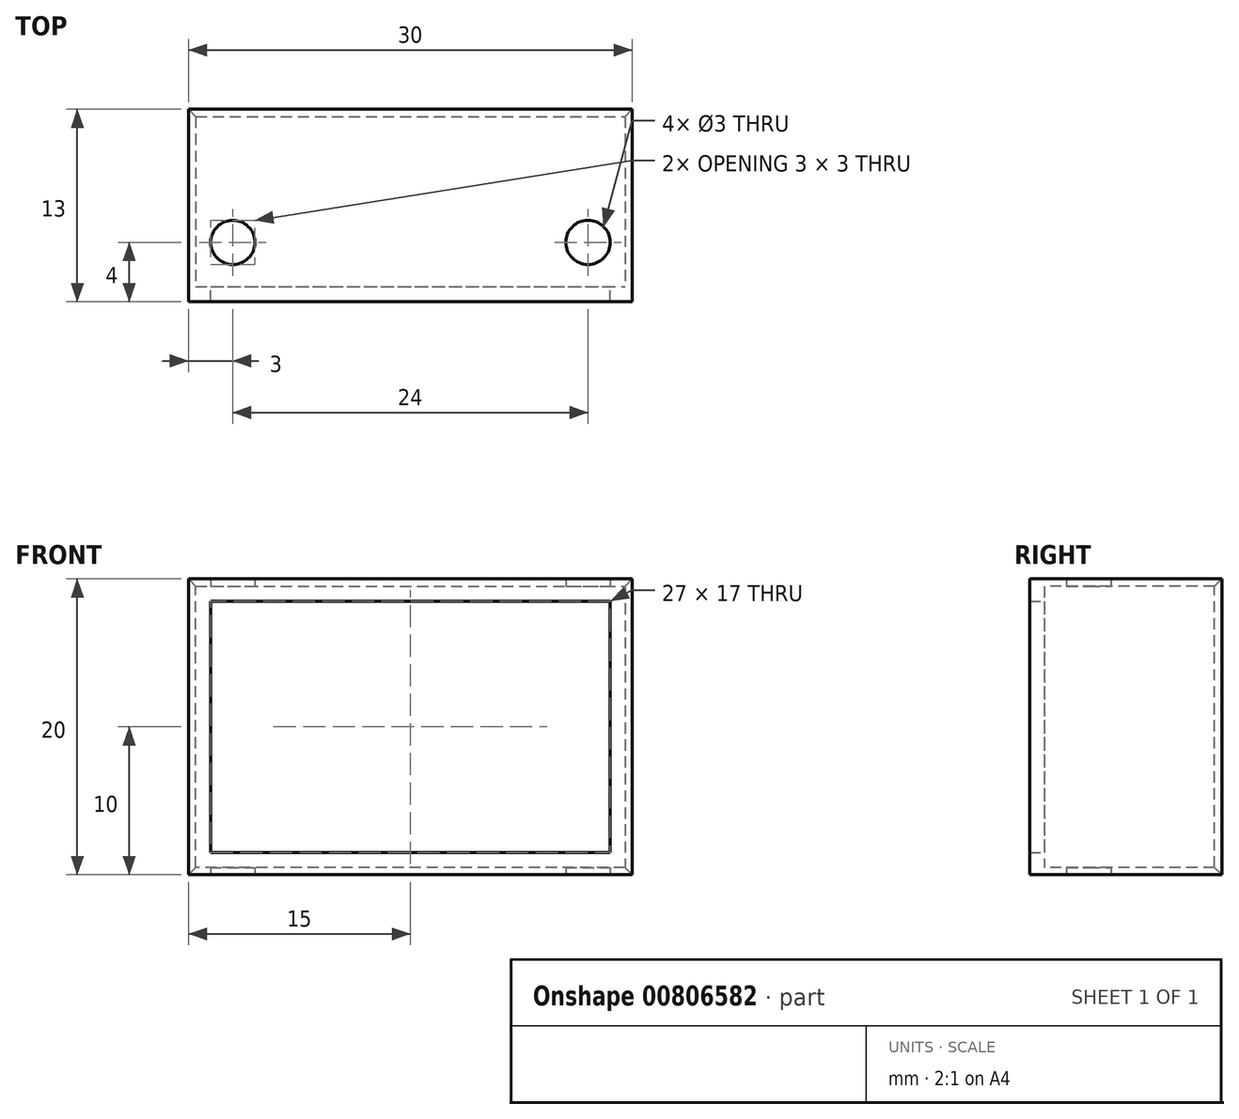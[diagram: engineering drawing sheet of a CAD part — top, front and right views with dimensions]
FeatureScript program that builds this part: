
annotation { "Feature Type Name" : "Feature", "Feature Type Description" : "" }
export const myFeature = defineFeature(function(context is Context, id is Id, definition is map)
    precondition{}
    {
        {
            var Q0;
            Q0=qCreatedBy(makeId("Top.planeOp"),FACE);
            var sketch = newSketch(context, id + "F0", { "sketchPlane" : qUnion([Q0])});
            skLineSegment(sketch, "E0.bottom", {"start": v(-15, 12) * mm, "end": v(15, 12) * mm});
            skLineSegment(sketch, "E0.top", {"start": v(-15, 0) * mm, "end": v(15, 0) * mm});
            skLineSegment(sketch, "E0.left", {"start": v(-15, 12) * mm, "end": v(-15, 0) * mm});
            skLineSegment(sketch, "E0.right", {"start": v(15, 12) * mm, "end": v(15, 0) * mm});
            skCircle(sketch, "E1", {"center": v(-12, 3) * mm, "radius": 1.5 * mm});
            skCircle(sketch, "E2", {"center": v(12, 3) * mm, "radius": 1.5 * mm});
            skSolve(sketch);
        }
        {
            var Q0;
            Q0=makeQuery(id+"F0.imprint","IMPRINT",FACE,{"disambiguationData":[TD([[makeQuery(id+"F0.imprint","IMPRINT",EDGE,{"derivedFrom":sQuery(id+"F0.wireOp",EDGE,"E0.bottom")}),-1.0]])]});
            extrude(context, id + "F1", {"entities" : qUnion([Q0]), "depth" : 20 * mm, "offsetDistance" : 25 * mm});
        }
        {
            var Q0;
            Q0=qCreatedBy(makeId("Front.planeOp"),FACE);
            var sketch = newSketch(context, id + "F2", { "sketchPlane" : qUnion([Q0])});
            skLineSegment(sketch, "E3.bottom", {"start": v(-14.5, 19.5) * mm, "end": v(14.5, 19.5) * mm});
            skLineSegment(sketch, "E3.top", {"start": v(-14.5, 0.5) * mm, "end": v(14.5, 0.5) * mm});
            skLineSegment(sketch, "E3.left", {"start": v(-14.5, 19.5) * mm, "end": v(-14.5, 0.5) * mm});
            skLineSegment(sketch, "E3.right", {"start": v(14.5, 19.5) * mm, "end": v(14.5, 0.5) * mm});
            skLineSegment(sketch, "E4.0", {"start": v(-13.5, 18.5) * mm, "end": v(13.5, 18.5) * mm});
            skLineSegment(sketch, "E4.1", {"start": v(-13.5, 18.5) * mm, "end": v(-13.5, 1.5) * mm});
            skLineSegment(sketch, "E4.2", {"start": v(-13.5, 1.5) * mm, "end": v(13.5, 1.5) * mm});
            skLineSegment(sketch, "E4.3", {"start": v(13.5, 18.5) * mm, "end": v(13.5, 1.5) * mm});
            skLineSegment(sketch, "E5.0", {"start": v(-15, 20) * mm, "end": v(15, 20) * mm});
            skLineSegment(sketch, "E5.1", {"start": v(-15, 20) * mm, "end": v(-15, 0) * mm});
            skLineSegment(sketch, "E5.2", {"start": v(-15, 0) * mm, "end": v(15, 0) * mm});
            skLineSegment(sketch, "E5.3", {"start": v(15, 20) * mm, "end": v(15, 0) * mm});
            skSolve(sketch);
        }
        {
            var Q0;
            Q0=makeQuery(id+"F2.imprint","IMPRINT",FACE,{"disambiguationData":[TD([[makeQuery(id+"F2.imprint","IMPRINT",EDGE,{"derivedFrom":sQuery(id+"F2.wireOp",EDGE,"E3.bottom")}),-1.0]])]});
            var Q1;
            Q1=makeQuery(id+"F2.imprint","IMPRINT",FACE,{"disambiguationData":[TD([[makeQuery(id+"F2.imprint","IMPRINT",EDGE,{"derivedFrom":sQuery(id+"F2.wireOp",EDGE,"E4.0")}),-1.0]])]});
            extrude(context, id + "F3", {"entities" : qUnion([Q0, Q1]), "operationType" : NewBodyOperationType.REMOVE, "oppositeDirection" : true, "depth" : 12 * mm, "offsetDistance" : 25 * mm});
        }
        {
            var Q0;
            Q0=makeQuery(id+"F2.imprint","IMPRINT",FACE,{"disambiguationData":[TD([[makeQuery(id+"F2.imprint","IMPRINT",EDGE,{"derivedFrom":sQuery(id+"F2.wireOp",EDGE,"E3.bottom")}),1.0]])]});
            var Q1;
            Q1=makeQuery(id+"F2.imprint","IMPRINT",FACE,{"disambiguationData":[TD([[makeQuery(id+"F2.imprint","IMPRINT",EDGE,{"derivedFrom":sQuery(id+"F2.wireOp",EDGE,"E3.bottom")}),-1.0]])]});
            extrude(context, id + "F4", {"entities" : qUnion([Q0, Q1]), "operationType" : NewBodyOperationType.ADD, "depth" : 1 * mm, "offsetDistance" : 25 * mm});
        }
        {
            var Q0;
            Q0=makeQuery(id+"F3.boolean.opBoolean","INTERSECT",EDGE,{"derivedFrom":[makeQuery(id+"F1.opExtrude","SWEPT_FACE",FACE,{"disambiguationData":[OSD([sQuery(id+"F0.wireOp",EDGE,"E0.bottom")])]}),makeQuery(id+"F3.opExtrude","SWEPT_FACE",FACE,{"disambiguationData":[OSD([sQuery(id+"F2.wireOp",EDGE,"E3.top")])]})]});
            var Q1;
            Q1=makeQuery(id+"F3.boolean.opBoolean","INTERSECT",EDGE,{"derivedFrom":[makeQuery(id+"F1.opExtrude","SWEPT_FACE",FACE,{"disambiguationData":[OSD([sQuery(id+"F0.wireOp",EDGE,"E0.bottom")])]}),makeQuery(id+"F3.opExtrude","SWEPT_FACE",FACE,{"disambiguationData":[OSD([sQuery(id+"F2.wireOp",EDGE,"E3.right")])]})]});
            var Q2;
            Q2=makeQuery(id+"F3.boolean.opBoolean","INTERSECT",EDGE,{"derivedFrom":[makeQuery(id+"F1.opExtrude","SWEPT_FACE",FACE,{"disambiguationData":[OSD([sQuery(id+"F0.wireOp",EDGE,"E0.bottom")])]}),makeQuery(id+"F3.opExtrude","SWEPT_FACE",FACE,{"disambiguationData":[OSD([sQuery(id+"F2.wireOp",EDGE,"E3.bottom")])]})]});
            var Q3;
            Q3=makeQuery(id+"F3.boolean.opBoolean","INTERSECT",EDGE,{"derivedFrom":[makeQuery(id+"F1.opExtrude","SWEPT_FACE",FACE,{"disambiguationData":[OSD([sQuery(id+"F0.wireOp",EDGE,"E0.bottom")])]}),makeQuery(id+"F3.opExtrude","SWEPT_FACE",FACE,{"disambiguationData":[OSD([sQuery(id+"F2.wireOp",EDGE,"E3.left")])]})]});
            chamfer(context, id + "F5", {"entities" : qUnion([Q0, Q1, Q2, Q3]), "chamferType" : ChamferType.OFFSET_ANGLE, "width" : 0.5 * mm, "oppositeDirection" : false, "angle" : 45 * degree, "tangentPropagation" : true});
        }
    });
